# Revit family: Atdec-Ceiling_Dislpay_Mount-TH-1040-CT-
name_source: partatom
category: Generic Models
revit_build: Autodesk Revit 2016 (Build: 20150220_1215(x64)
units: mm (PartAtom-declared; Revit-internal decimal feet)

## family parameters
Can host rebar = No
Cut with Voids When Loaded = No
Host = Face
Part Type = Normal
Room Calculation Point = No
Round Connector Dimension = Use Diameter
Shared = No

## types (2) — shared parameters
Assembly Code = E1010800
Colour Options = Black
Default Elevation = 1219 mm
Flat screen maximum supported weight = 25kg (55lb)
Manufacturer = Atdec
Material = Steel and Aluminum
Maximum distance from wall (mm) = -
Minimum distance from wall (mm) = -
Pan adjustment = 20° of display adjustment in any direction
Product Family = Wall Mount Rail
Product Information Link = https://www.atdec.com.au
Range Of Motion = Tilt
Security features = Security screw to deter unauthorised removal
Tilt adjustment = 20° of display adjustment in any direction
URL = www.atdec.com.au
Universal Height (mm) = -
Universal Width (mm) = -
VESA mounting hole pattern, mm = 75x75, 100x100, 200x100, 200x200
Warranty = 10 years

## per-type parameters (varying)
| type | CTL | CTS | Description | Low Pole Length | Master Carton Dimensions | Single Unit Dimensions | Single units per master pack | Top Pole Length | UPC Code | Weight, master carton | Weight, single unit |
| TH-1040-CTL | Yes | No | Medium size display mount 900mm to 1800mm | 868 mm  [stored 2.84777 ft] | 1015mm (40") Lenght, 255mm (10") Width, 225mm (8.9") Height | 1005mm (39.4") Lenght, 240mm (9.4") Width, 100mm (3.9") Height | 2 | 1000 mm  [stored 3.28084 ft] | 881493006010 | 17.7kg (38.9lb) | 8.5 kg (18.7lb) |
| TH-1040-CTS | No | Yes | Medium size display mount 400mm to 900mm | 450 mm  [stored 1.47638 ft] | 570mm (22.4") Lenght, 250mm (9.8") Width, 330mm (13") Height | 555mm (21.9") Lenght, 240mm (9.4") Width, 100mm (3.9") Height | 3 | 450 mm  [stored 1.47638 ft] | 881493005990 | 17kg (37.4lb) | 5.5 kg (12lb) |

note: column(s) folded — value = type name in every type: Model

note: [stored X ft] marks values corroborated as IEEE doubles in the binary element streams (Revit-internal decimal feet)

## geometry (parser evidence)
native form markers: Sweep x3
no freeform markers — native parametric forms only
